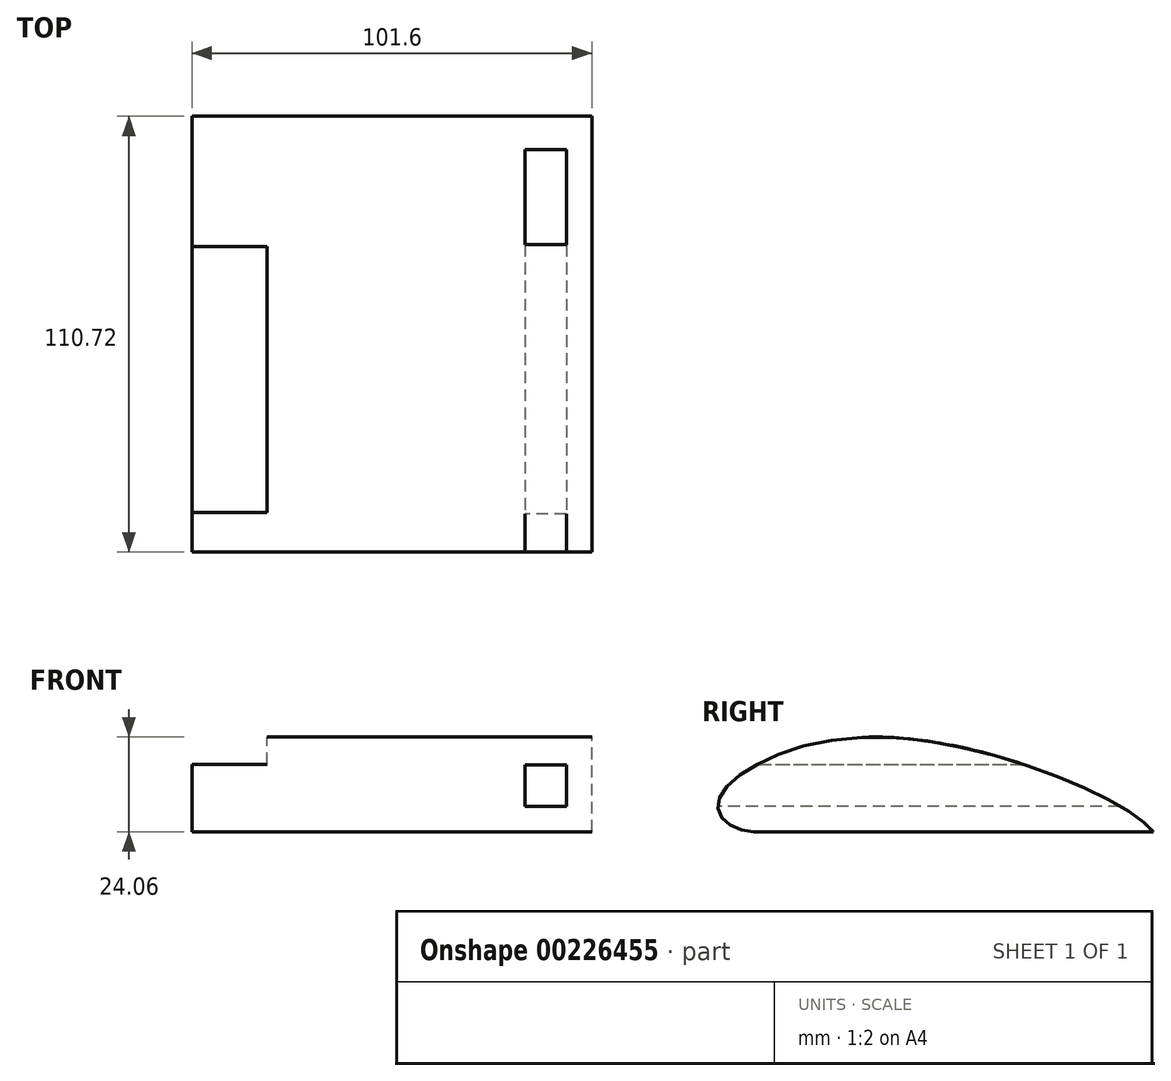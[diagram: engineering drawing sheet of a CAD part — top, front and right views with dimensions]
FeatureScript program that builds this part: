
annotation { "Feature Type Name" : "Feature", "Feature Type Description" : "" }
export const myFeature = defineFeature(function(context is Context, id is Id, definition is map)
    precondition{}
    {
        {
            var Q0;
            Q0=qCreatedBy(makeId("Right.planeOp"),FACE);
            var sketch = newSketch(context, id + "F0", { "sketchPlane" : qUnion([Q0])});
            skLineSegment(sketch, "E0", {"start": v(-58.7, 0) * mm, "end": v(42.9, 0) * mm});
            skFitSpline(sketch, "E1", {"points": [v(-58.7, 0) * mm, v(-67.81, 6.21) * mm, v(-30.38, 24.02) * mm, v(42.9, 0) * mm], "startDerivative": vector(-72.15, 0) * mm, "endDerivative": vector(37.52, -50.47) * mm});
            skSolve(sketch);
        }
        {
            var Q0;
            Q0 = qSketchRegion(id + "F0", true);
            extrude(context, id + "F1", {"entities" : qUnion([Q0]), "depth" : 101.6 * mm, "symmetric" : true});
        }
        {
            var Q0;
            Q0=qCreatedBy(makeId("Front.planeOp"),FACE);
            var sketch = newSketch(context, id + "F2", { "sketchPlane" : qUnion([Q0])});
            skLineSegment(sketch, "E2.bottom", {"start": v(44.33, 6.47) * mm, "end": v(33.83, 6.47) * mm});
            skLineSegment(sketch, "E2.top", {"start": v(44.33, 16.97) * mm, "end": v(33.83, 16.97) * mm});
            skLineSegment(sketch, "E2.left", {"start": v(44.33, 6.47) * mm, "end": v(44.33, 16.97) * mm});
            skLineSegment(sketch, "E2.right", {"start": v(33.83, 6.47) * mm, "end": v(33.83, 16.97) * mm});
            skPoint(sketch, "E2.middle", {"position": v(39.08, 11.72) * mm});
            skFitSpline(sketch, "E3.0", {"points": [v(63.5, 0) * mm, v(63.5, 8.17) * mm, v(63.5, 16.34) * mm, v(63.5, 24.51) * mm]});
            skLineSegment(sketch, "E4", {"start": v(39.08, 11.72) * mm, "end": v(50.8, 11.72) * mm, "construction": true});
            skLineSegment(sketch, "E5", {"start": v(39.08, 11.72) * mm, "end": v(39.08, 0) * mm, "construction": true});
            skPoint(sketch, "E5.endSnap0", {"position": v(39.08, 6.47) * mm});
            skSolve(sketch);
        }
        {
            var Q0;
            Q0 = qSketchRegion(id + "F2", true);
            extrude(context, id + "F3", {"entities" : qUnion([Q0]), "operationType" : NewBodyOperationType.REMOVE, "oppositeDirection" : true, "depth" : 584.2 * mm, "symmetric" : true});
        }
        {
            var Q0;
            Q0=qCreatedBy(makeId("Top.planeOp"),FACE);
            cPlane(context, id + "F4", {"entities" : qUnion([Q0]), "cplaneType" : CPlaneType.OFFSET, "offset" : 25.4 * mm, "width" : 152.4 * mm, "height" : 152.4 * mm});
        }
        {
            var Q0;
            Q0=qCreatedBy(id+"F4.planeOp",FACE);
            var sketch = newSketch(context, id + "F5", { "sketchPlane" : qUnion([Q0])});
            skLineSegment(sketch, "E6.bottom", {"start": v(-31.75, -58.7) * mm, "end": v(-50.8, -58.7) * mm});
            skLineSegment(sketch, "E6.top", {"start": v(-31.75, 42.9) * mm, "end": v(-50.8, 42.9) * mm});
            skLineSegment(sketch, "E6.left", {"start": v(-31.75, -58.7) * mm, "end": v(-31.75, 42.9) * mm});
            skLineSegment(sketch, "E6.right", {"start": v(-50.8, -58.7) * mm, "end": v(-50.8, 42.9) * mm});
            skPoint(sketch, "E6.middle", {"position": v(-41.27, -7.9) * mm});
            skSolve(sketch);
        }
        {
            var Q0;
            Q0 = qSketchRegion(id + "F5", true);
            extrude(context, id + "F6", {"entities" : qUnion([Q0]), "operationType" : NewBodyOperationType.REMOVE, "oppositeDirection" : true, "depth" : 8.25 * mm});
        }
    });
